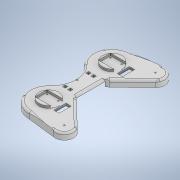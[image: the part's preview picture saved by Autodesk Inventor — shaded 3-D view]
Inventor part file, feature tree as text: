
AUTODESK INVENTOR PART (.ipt)
format: ipt  version: 2021 (Build 250183000, 183)  size: 491,520 bytes
history: native  units: mm
features: sketch x11, extrude x10, fillet x3, other x1
ambient origin geometry x8: Origin, YZ Plane, XZ Plane, XY Plane, X Axis, Y Axis, Z Axis, Center Point
bodies: Body1 (feature_tree)
feature tree (25):
  other  "Sólido1"
  extrude  "Extrusión1"  Depth=10.0mm TaperAngle=0.0deg
  extrude  "Extrusión2"  Depth=5.0mm TaperAngle=0.0deg
  extrude  "Extrusión3"  Depth=5.0mm
  extrude  "Extrusión4"  Depth=15.0mm TaperAngle=0.0deg
  extrude  "Extrusión5"  Depth=10.0mm TaperAngle=0.0deg
  fillet  "Empalme1"  Radius=20.0mm
  extrude  "Extrusión6"  Depth=4.0mm
  extrude  "Extrusión7"  Depth=30.0mm
  extrude  "Extrusión8"  Depth=10.0mm
  sketch  "Boceto9"  dims[d56=0.872665mm]
  extrude  "Extrusión9"  [1 undecoded]
  fillet  "Empalme2"  [1 undecoded]
  fillet  "Empalme3"  [1 undecoded]
  extrude  "Extrusión10"  [1 undecoded]
  sketch  "Boceto1"  dims[d21=5.0mm d22=0.0mm d25=10.0mm d26=0.0mm]
  sketch  "Boceto2"  dims[d27=5.0mm d28=0.0mm d29=5.0mm d30=0.0mm]
  sketch  "Boceto3"  dims[d41=15.0mm d42=0.0mm d43=5.0mm]
  sketch  "Boceto4"  dims[d45=12.0mm d46=15.0mm d47=0.0mm]
  sketch  "Boceto5"  dims[d53=16.0mm d54=0.0mm d64=10.0mm d65=0.0mm d66=20.0mm d67=0.0mm]
  sketch  "Boceto6"  dims[d68=4.0mm d69=4.0mm]
  sketch  "Boceto7"  dims[d70=30.0mm d71=30.0mm]
  sketch  "Boceto8"  dims[d72=10.0mm d73=0.0mm d55=0.5mm]
  sketch  "Boceto10"
  sketch  "Boceto11"
note: 4 required parameter values undecoded (feature->parameter linkage not recoverable at this tier; creation-order binding heuristic only, values carry confidence <= 0.55)
